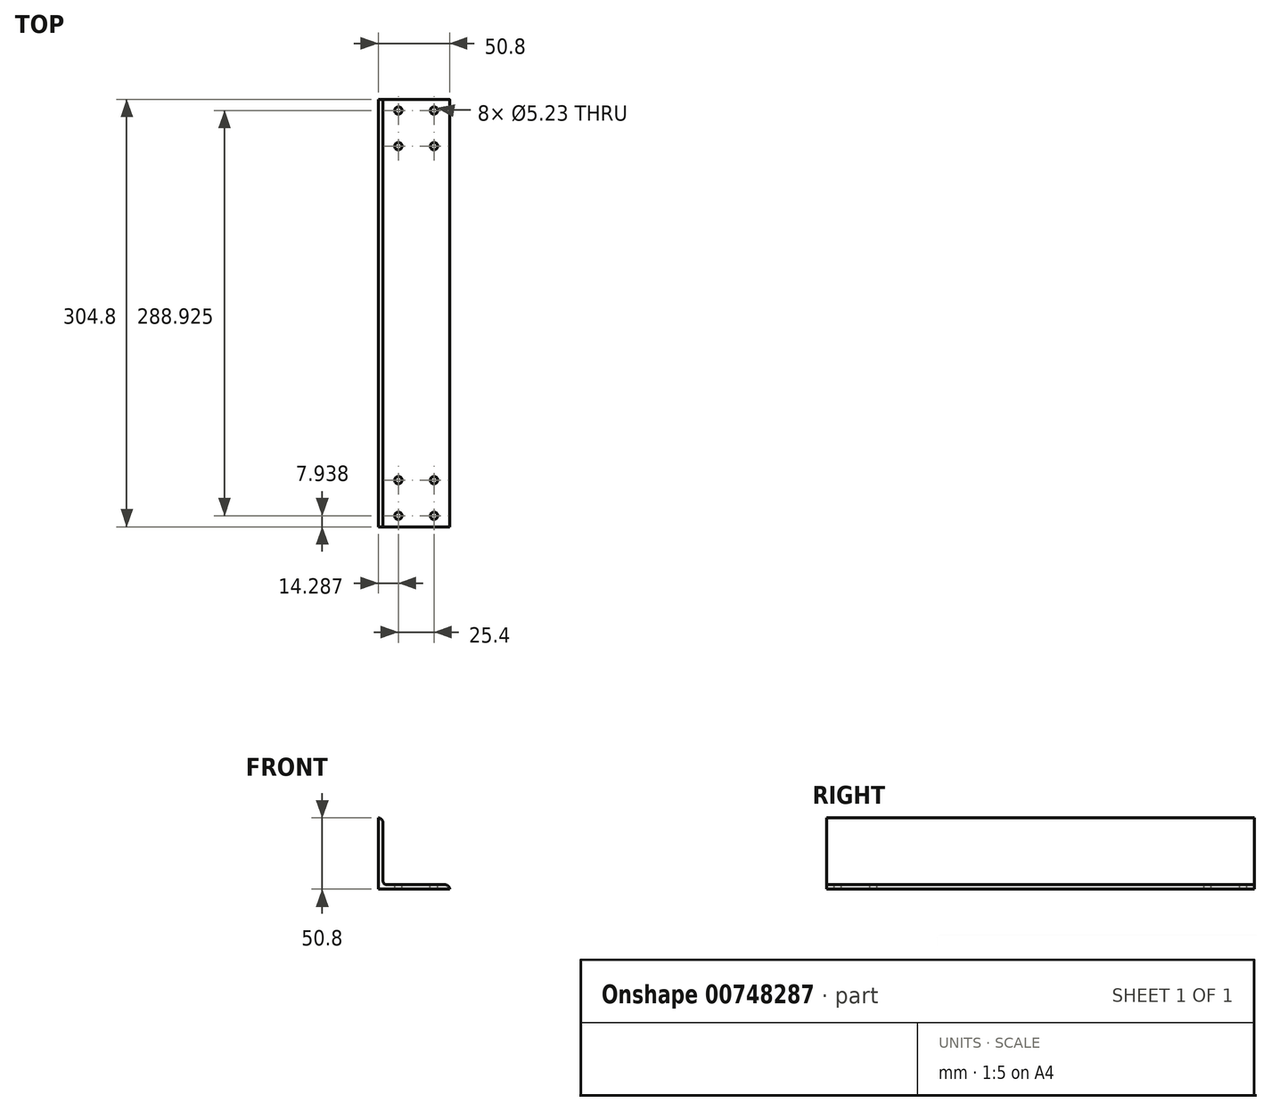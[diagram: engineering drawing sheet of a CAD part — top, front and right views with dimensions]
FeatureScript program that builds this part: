
annotation { "Feature Type Name" : "Feature", "Feature Type Description" : "" }
export const myFeature = defineFeature(function(context is Context, id is Id, definition is map)
    precondition{}
    {
        {
            var Q0;
            Q0=qCreatedBy(makeId("Front.planeOp"),FACE);
            var sketch = newSketch(context, id + "F0", { "sketchPlane" : qUnion([Q0])});
            skLineSegment(sketch, "E0", {"start": v(0, 0) * mm, "end": v(-50.8, 0) * mm});
            skLineSegment(sketch, "E1", {"start": v(-50.8, 0) * mm, "end": v(-50.8, 50.8) * mm});
            skLineSegment(sketch, "E2", {"start": v(-50.8, 50.8) * mm, "end": v(-50.8, 50.8) * mm});
            skLineSegment(sketch, "E3", {"start": v(-47.63, 47.63) * mm, "end": v(-47.63, 6.35) * mm});
            skLineSegment(sketch, "E4", {"start": v(-44.45, 3.18) * mm, "end": v(-3.18, 3.18) * mm});
            skLineSegment(sketch, "E5", {"start": v(0, 0) * mm, "end": v(0, 0) * mm});
            skPoint(sketch, "E6.visualSharp", {"position": v(-47.63, 3.18) * mm});
            skArc(sketch, "E6.filletArc", {"start": v(-47.63, 6.35) * mm, "mid": v(-46.7, 4.1) * mm, "end": v(-44.45, 3.18) * mm});
            skPoint(sketch, "E7.visualSharp", {"position": v(-47.63, 50.8) * mm});
            skArc(sketch, "E7.filletArc", {"start": v(-47.63, 47.63) * mm, "mid": v(-48.55, 49.87) * mm, "end": v(-50.8, 50.8) * mm});
            skPoint(sketch, "E8.visualSharp", {"position": v(0, 3.18) * mm});
            skArc(sketch, "E8.filletArc", {"start": v(0, 0) * mm, "mid": v(-0.93, 2.25) * mm, "end": v(-3.18, 3.18) * mm});
            skSolve(sketch);
        }
        {
            var Q0;
            Q0=qSketchRegion(id+"F0",true);
            extrude(context, id + "F1", {"entities" : qUnion([Q0]), "depth" : 304.8 * mm, "offsetDistance" : 25.4 * mm});
        }
        {
            var Q0;
            Q0=makeQuery(id+"F1.opExtrude","SWEPT_FACE",FACE,{"disambiguationData":[OSD([sQuery(id+"F0.wireOp",EDGE,"E4")])]});
            var sketch = newSketch(context, id + "F2", { "sketchPlane" : qUnion([Q0])});
            skLineSegment(sketch, "E9", {"start": v(-23.81, -304.8) * mm, "end": v(-23.81, 0) * mm, "construction": true});
            skLineSegment(sketch, "E10", {"start": v(-3.17, -296.86) * mm, "end": v(-44.45, -296.86) * mm, "construction": true});
            skCircle(sketch, "E11", {"center": v(-36.51, -296.86) * mm, "radius": 2.62 * mm});
            skLineSegment(sketch, "E12", {"start": v(-44.45, -7.94) * mm, "end": v(-3.18, -7.94) * mm, "construction": true});
            skCircle(sketch, "E13", {"center": v(-36.51, -7.94) * mm, "radius": 2.62 * mm});
            skLineSegment(sketch, "E14", {"start": v(-36.51, -304.8) * mm, "end": v(-36.51, 0) * mm, "construction": true});
            skLineSegment(sketch, "E15", {"start": v(-44.45, -271.46) * mm, "end": v(-3.17, -271.46) * mm, "construction": true});
            skLineSegment(sketch, "E16", {"start": v(-11.11, -304.8) * mm, "end": v(-11.11, 0) * mm, "construction": true});
            skLineSegment(sketch, "E17", {"start": v(-44.45, -33.34) * mm, "end": v(-3.17, -33.34) * mm, "construction": true});
            skCircle(sketch, "E18", {"center": v(-11.11, -7.94) * mm, "radius": 2.62 * mm});
            skCircle(sketch, "E19", {"center": v(-36.51, -33.34) * mm, "radius": 2.62 * mm});
            skCircle(sketch, "E20", {"center": v(-11.11, -33.34) * mm, "radius": 2.62 * mm});
            skCircle(sketch, "E21", {"center": v(-36.51, -271.46) * mm, "radius": 2.62 * mm});
            skCircle(sketch, "E22", {"center": v(-11.11, -296.86) * mm, "radius": 2.62 * mm});
            skCircle(sketch, "E23", {"center": v(-11.11, -271.46) * mm, "radius": 2.62 * mm});
            skSolve(sketch);
        }
        {
            var Q0;
            Q0=qSketchRegion(id+"F2",true);
            extrude(context, id + "F3", {"entities" : qUnion([Q0]), "operationType" : NewBodyOperationType.REMOVE, "endBound" : BoundingType.THROUGH_ALL, "oppositeDirection" : true, "depth" : 25.4 * mm, "offsetDistance" : 25.4 * mm});
        }
    });
